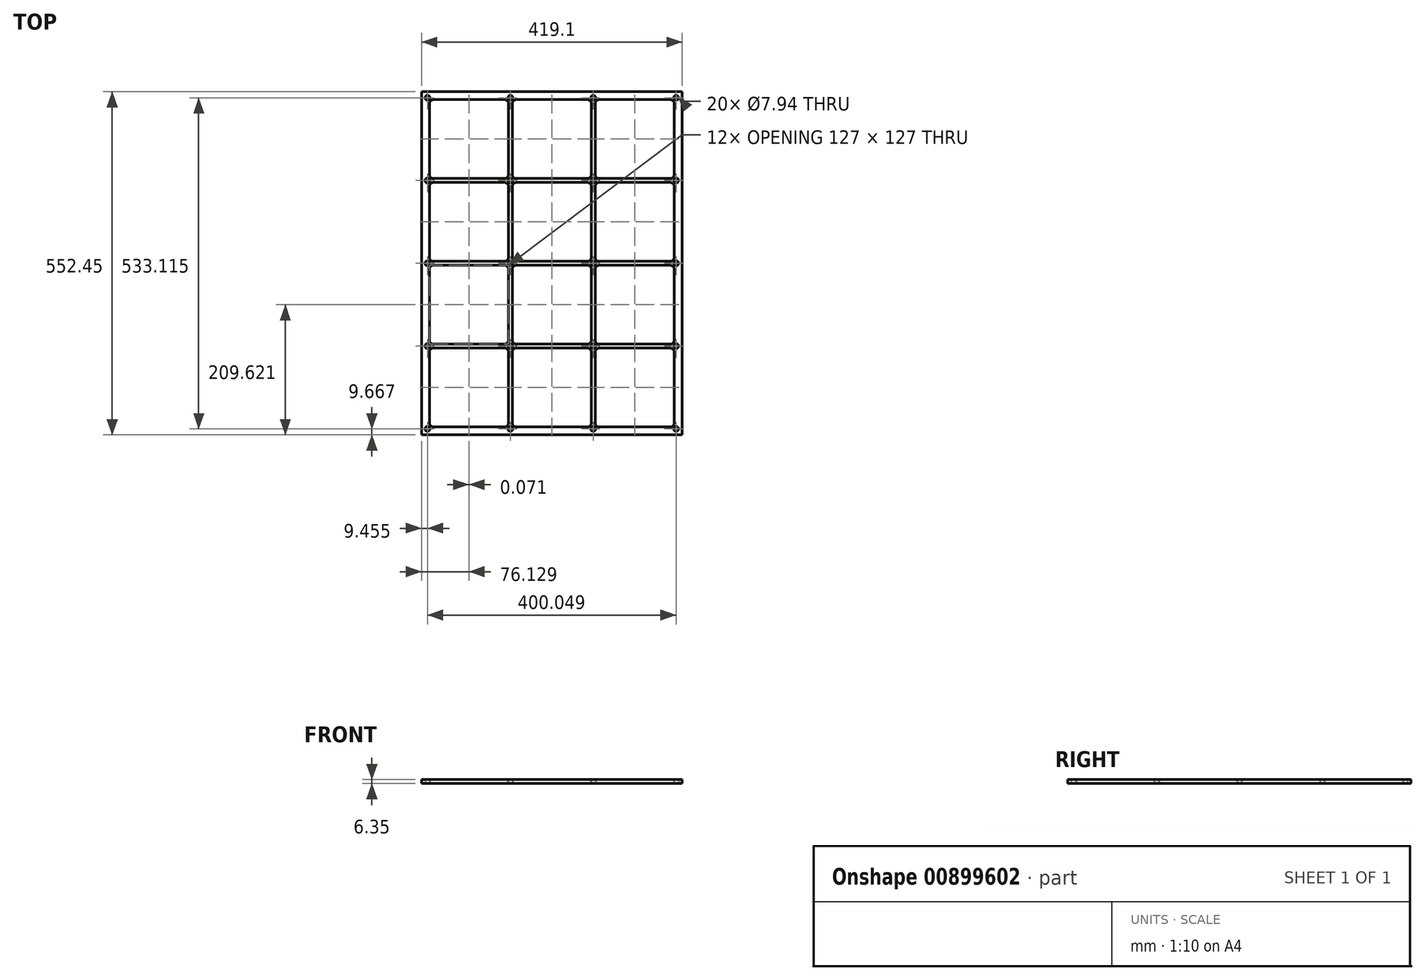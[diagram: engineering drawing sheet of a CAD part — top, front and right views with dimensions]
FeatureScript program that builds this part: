
annotation { "Feature Type Name" : "Feature", "Feature Type Description" : "" }
export const myFeature = defineFeature(function(context is Context, id is Id, definition is map)
    precondition{}
    {
        {
            var Q0;
            Q0=qCreatedBy(makeId("Top.planeOp"),FACE);
            var sketch = newSketch(context, id + "F0", { "sketchPlane" : qUnion([Q0])});
            skLineSegment(sketch, "E0.bottom", {"start": v(19.05, 12.84) * mm, "end": v(133.35, 12.84) * mm});
            skLineSegment(sketch, "E0.top", {"start": v(19.05, 139.84) * mm, "end": v(133.35, 139.84) * mm});
            skLineSegment(sketch, "E0.left", {"start": v(12.7, 19.2) * mm, "end": v(12.7, 133.5) * mm});
            skLineSegment(sketch, "E0.right", {"start": v(139.7, 19.2) * mm, "end": v(139.7, 133.5) * mm});
            skArc(sketch, "E1.filletArc", {"start": v(19.05, 139.84) * mm, "mid": v(14.56, 137.98) * mm, "end": v(12.7, 133.5) * mm});
            skArc(sketch, "E2.filletArc", {"start": v(139.7, 133.5) * mm, "mid": v(137.84, 137.98) * mm, "end": v(133.35, 139.84) * mm});
            skArc(sketch, "E3.filletArc", {"start": v(133.35, 12.84) * mm, "mid": v(137.84, 14.7) * mm, "end": v(139.7, 19.2) * mm});
            skArc(sketch, "E4.filletArc", {"start": v(12.7, 19.2) * mm, "mid": v(14.56, 14.7) * mm, "end": v(19.05, 12.84) * mm});
            skLineSegment(sketch, "E5.0.1.1", {"start": v(139.63, 152.47) * mm, "end": v(139.63, 266.77) * mm});
            skLineSegment(sketch, "E5.0.1.2", {"start": v(18.98, 146.12) * mm, "end": v(133.28, 146.12) * mm});
            skLineSegment(sketch, "E5.0.1.4", {"start": v(18.98, 273.12) * mm, "end": v(133.28, 273.12) * mm});
            skLineSegment(sketch, "E5.0.1.5", {"start": v(12.63, 152.47) * mm, "end": v(12.63, 266.77) * mm});
            skArc(sketch, "E5.0.1.8", {"start": v(139.63, 266.77) * mm, "mid": v(137.77, 271.26) * mm, "end": v(133.28, 273.12) * mm});
            skArc(sketch, "E5.0.1.9", {"start": v(18.98, 273.12) * mm, "mid": v(14.49, 271.26) * mm, "end": v(12.63, 266.77) * mm});
            skArc(sketch, "E5.0.1.10", {"start": v(12.63, 152.47) * mm, "mid": v(14.49, 147.98) * mm, "end": v(18.98, 146.12) * mm});
            skArc(sketch, "E5.0.1.11", {"start": v(133.28, 146.12) * mm, "mid": v(137.77, 147.98) * mm, "end": v(139.63, 152.47) * mm});
            skLineSegment(sketch, "E5.0.2.1", {"start": v(139.7, 285.75) * mm, "end": v(139.7, 400.05) * mm});
            skLineSegment(sketch, "E5.0.2.2", {"start": v(19.05, 279.4) * mm, "end": v(133.35, 279.4) * mm});
            skLineSegment(sketch, "E5.0.2.4", {"start": v(19.05, 406.4) * mm, "end": v(133.35, 406.4) * mm});
            skLineSegment(sketch, "E5.0.2.5", {"start": v(12.7, 285.75) * mm, "end": v(12.7, 400.05) * mm});
            skArc(sketch, "E5.0.2.8", {"start": v(139.7, 400.05) * mm, "mid": v(137.84, 404.54) * mm, "end": v(133.35, 406.4) * mm});
            skArc(sketch, "E5.0.2.9", {"start": v(19.05, 406.4) * mm, "mid": v(14.56, 404.54) * mm, "end": v(12.7, 400.05) * mm});
            skArc(sketch, "E5.0.2.10", {"start": v(12.7, 285.75) * mm, "mid": v(14.56, 281.26) * mm, "end": v(19.05, 279.4) * mm});
            skArc(sketch, "E5.0.2.11", {"start": v(133.35, 279.4) * mm, "mid": v(137.84, 281.26) * mm, "end": v(139.7, 285.75) * mm});
            skLineSegment(sketch, "E5.0.3.1", {"start": v(139.7, 419.1) * mm, "end": v(139.7, 533.4) * mm});
            skLineSegment(sketch, "E5.0.3.2", {"start": v(19.05, 412.75) * mm, "end": v(133.35, 412.75) * mm});
            skLineSegment(sketch, "E5.0.3.4", {"start": v(19.05, 539.75) * mm, "end": v(133.35, 539.75) * mm});
            skLineSegment(sketch, "E5.0.3.5", {"start": v(12.7, 419.1) * mm, "end": v(12.7, 533.4) * mm});
            skArc(sketch, "E5.0.3.8", {"start": v(139.7, 533.4) * mm, "mid": v(137.84, 537.9) * mm, "end": v(133.35, 539.75) * mm});
            skArc(sketch, "E5.0.3.9", {"start": v(19.05, 539.75) * mm, "mid": v(14.56, 537.9) * mm, "end": v(12.7, 533.4) * mm});
            skArc(sketch, "E5.0.3.10", {"start": v(12.7, 419.1) * mm, "mid": v(14.56, 414.6) * mm, "end": v(19.05, 412.75) * mm});
            skArc(sketch, "E5.0.3.11", {"start": v(133.35, 412.75) * mm, "mid": v(137.84, 414.6) * mm, "end": v(139.7, 419.1) * mm});
            skLineSegment(sketch, "E5.1.0.1", {"start": v(272.98, 19.12) * mm, "end": v(272.98, 133.42) * mm});
            skLineSegment(sketch, "E5.1.0.2", {"start": v(152.33, 12.77) * mm, "end": v(266.63, 12.77) * mm});
            skLineSegment(sketch, "E5.1.0.4", {"start": v(152.33, 139.77) * mm, "end": v(266.63, 139.77) * mm});
            skLineSegment(sketch, "E5.1.0.5", {"start": v(145.98, 19.12) * mm, "end": v(145.98, 133.42) * mm});
            skArc(sketch, "E5.1.0.8", {"start": v(272.98, 133.42) * mm, "mid": v(271.12, 137.91) * mm, "end": v(266.63, 139.77) * mm});
            skArc(sketch, "E5.1.0.9", {"start": v(152.33, 139.77) * mm, "mid": v(147.84, 137.91) * mm, "end": v(145.98, 133.42) * mm});
            skArc(sketch, "E5.1.0.10", {"start": v(145.98, 19.12) * mm, "mid": v(147.84, 14.63) * mm, "end": v(152.33, 12.77) * mm});
            skArc(sketch, "E5.1.0.11", {"start": v(266.63, 12.77) * mm, "mid": v(271.12, 14.63) * mm, "end": v(272.98, 19.12) * mm});
            skLineSegment(sketch, "E5.1.1.1", {"start": v(273.05, 152.54) * mm, "end": v(273.05, 266.84) * mm});
            skLineSegment(sketch, "E5.1.1.2", {"start": v(152.4, 146.2) * mm, "end": v(266.7, 146.2) * mm});
            skLineSegment(sketch, "E5.1.1.4", {"start": v(152.4, 273.2) * mm, "end": v(266.7, 273.2) * mm});
            skLineSegment(sketch, "E5.1.1.5", {"start": v(146.05, 152.54) * mm, "end": v(146.05, 266.84) * mm});
            skArc(sketch, "E5.1.1.8", {"start": v(273.05, 266.84) * mm, "mid": v(271.2, 271.33) * mm, "end": v(266.7, 273.2) * mm});
            skArc(sketch, "E5.1.1.9", {"start": v(152.4, 273.2) * mm, "mid": v(147.9, 271.33) * mm, "end": v(146.05, 266.84) * mm});
            skArc(sketch, "E5.1.1.10", {"start": v(146.05, 152.54) * mm, "mid": v(147.9, 148.05) * mm, "end": v(152.4, 146.2) * mm});
            skArc(sketch, "E5.1.1.11", {"start": v(266.7, 146.2) * mm, "mid": v(271.2, 148.05) * mm, "end": v(273.05, 152.54) * mm});
            skLineSegment(sketch, "E5.1.2.1", {"start": v(273.05, 285.75) * mm, "end": v(273.05, 400.05) * mm});
            skLineSegment(sketch, "E5.1.2.2", {"start": v(152.4, 279.4) * mm, "end": v(266.7, 279.4) * mm});
            skLineSegment(sketch, "E5.1.2.4", {"start": v(152.4, 406.4) * mm, "end": v(266.7, 406.4) * mm});
            skLineSegment(sketch, "E5.1.2.5", {"start": v(146.05, 285.75) * mm, "end": v(146.05, 400.05) * mm});
            skArc(sketch, "E5.1.2.8", {"start": v(273.05, 400.05) * mm, "mid": v(271.2, 404.54) * mm, "end": v(266.7, 406.4) * mm});
            skArc(sketch, "E5.1.2.9", {"start": v(152.4, 406.4) * mm, "mid": v(147.9, 404.54) * mm, "end": v(146.05, 400.05) * mm});
            skArc(sketch, "E5.1.2.10", {"start": v(146.05, 285.75) * mm, "mid": v(147.9, 281.26) * mm, "end": v(152.4, 279.4) * mm});
            skArc(sketch, "E5.1.2.11", {"start": v(266.7, 279.4) * mm, "mid": v(271.2, 281.26) * mm, "end": v(273.05, 285.75) * mm});
            skLineSegment(sketch, "E5.1.3.1", {"start": v(273.05, 419.1) * mm, "end": v(273.05, 533.4) * mm});
            skLineSegment(sketch, "E5.1.3.2", {"start": v(152.4, 412.75) * mm, "end": v(266.7, 412.75) * mm});
            skLineSegment(sketch, "E5.1.3.4", {"start": v(152.4, 539.75) * mm, "end": v(266.7, 539.75) * mm});
            skLineSegment(sketch, "E5.1.3.5", {"start": v(146.05, 419.1) * mm, "end": v(146.05, 533.4) * mm});
            skArc(sketch, "E5.1.3.8", {"start": v(273.05, 533.4) * mm, "mid": v(271.2, 537.9) * mm, "end": v(266.7, 539.75) * mm});
            skArc(sketch, "E5.1.3.9", {"start": v(152.4, 539.75) * mm, "mid": v(147.9, 537.9) * mm, "end": v(146.05, 533.4) * mm});
            skArc(sketch, "E5.1.3.10", {"start": v(146.05, 419.1) * mm, "mid": v(147.9, 414.6) * mm, "end": v(152.4, 412.75) * mm});
            skArc(sketch, "E5.1.3.11", {"start": v(266.7, 412.75) * mm, "mid": v(271.2, 414.6) * mm, "end": v(273.05, 419.1) * mm});
            skLineSegment(sketch, "E5.2.0.1", {"start": v(406.4, 19.05) * mm, "end": v(406.4, 133.35) * mm});
            skLineSegment(sketch, "E5.2.0.2", {"start": v(285.75, 12.7) * mm, "end": v(400.05, 12.7) * mm});
            skLineSegment(sketch, "E5.2.0.4", {"start": v(285.75, 139.7) * mm, "end": v(400.05, 139.7) * mm});
            skLineSegment(sketch, "E5.2.0.5", {"start": v(279.4, 19.05) * mm, "end": v(279.4, 133.35) * mm});
            skArc(sketch, "E5.2.0.8", {"start": v(406.4, 133.35) * mm, "mid": v(404.54, 137.84) * mm, "end": v(400.05, 139.7) * mm});
            skArc(sketch, "E5.2.0.9", {"start": v(285.75, 139.7) * mm, "mid": v(281.26, 137.84) * mm, "end": v(279.4, 133.35) * mm});
            skArc(sketch, "E5.2.0.10", {"start": v(279.4, 19.05) * mm, "mid": v(281.26, 14.56) * mm, "end": v(285.75, 12.7) * mm});
            skArc(sketch, "E5.2.0.11", {"start": v(400.05, 12.7) * mm, "mid": v(404.54, 14.56) * mm, "end": v(406.4, 19.05) * mm});
            skLineSegment(sketch, "E5.2.1.1", {"start": v(406.4, 152.4) * mm, "end": v(406.4, 266.7) * mm});
            skLineSegment(sketch, "E5.2.1.2", {"start": v(285.75, 146.05) * mm, "end": v(400.05, 146.05) * mm});
            skLineSegment(sketch, "E5.2.1.4", {"start": v(285.75, 273.05) * mm, "end": v(400.05, 273.05) * mm});
            skLineSegment(sketch, "E5.2.1.5", {"start": v(279.4, 152.4) * mm, "end": v(279.4, 266.7) * mm});
            skArc(sketch, "E5.2.1.8", {"start": v(406.4, 266.7) * mm, "mid": v(404.54, 271.2) * mm, "end": v(400.05, 273.05) * mm});
            skArc(sketch, "E5.2.1.9", {"start": v(285.75, 273.05) * mm, "mid": v(281.26, 271.2) * mm, "end": v(279.4, 266.7) * mm});
            skArc(sketch, "E5.2.1.10", {"start": v(279.4, 152.4) * mm, "mid": v(281.26, 147.9) * mm, "end": v(285.75, 146.05) * mm});
            skArc(sketch, "E5.2.1.11", {"start": v(400.05, 146.05) * mm, "mid": v(404.54, 147.9) * mm, "end": v(406.4, 152.4) * mm});
            skLineSegment(sketch, "E5.2.2.1", {"start": v(406.4, 285.75) * mm, "end": v(406.4, 400.05) * mm});
            skLineSegment(sketch, "E5.2.2.2", {"start": v(285.75, 279.4) * mm, "end": v(400.05, 279.4) * mm});
            skLineSegment(sketch, "E5.2.2.4", {"start": v(285.75, 406.4) * mm, "end": v(400.05, 406.4) * mm});
            skLineSegment(sketch, "E5.2.2.5", {"start": v(279.4, 285.75) * mm, "end": v(279.4, 400.05) * mm});
            skArc(sketch, "E5.2.2.8", {"start": v(406.4, 400.05) * mm, "mid": v(404.54, 404.54) * mm, "end": v(400.05, 406.4) * mm});
            skArc(sketch, "E5.2.2.9", {"start": v(285.75, 406.4) * mm, "mid": v(281.26, 404.54) * mm, "end": v(279.4, 400.05) * mm});
            skArc(sketch, "E5.2.2.10", {"start": v(279.4, 285.75) * mm, "mid": v(281.26, 281.26) * mm, "end": v(285.75, 279.4) * mm});
            skArc(sketch, "E5.2.2.11", {"start": v(400.05, 279.4) * mm, "mid": v(404.54, 281.26) * mm, "end": v(406.4, 285.75) * mm});
            skLineSegment(sketch, "E5.2.3.1", {"start": v(406.4, 419.1) * mm, "end": v(406.4, 533.4) * mm});
            skLineSegment(sketch, "E5.2.3.2", {"start": v(285.75, 412.75) * mm, "end": v(400.05, 412.75) * mm});
            skLineSegment(sketch, "E5.2.3.4", {"start": v(285.75, 539.75) * mm, "end": v(400.05, 539.75) * mm});
            skLineSegment(sketch, "E5.2.3.5", {"start": v(279.4, 419.1) * mm, "end": v(279.4, 533.4) * mm});
            skArc(sketch, "E5.2.3.8", {"start": v(406.4, 533.4) * mm, "mid": v(404.54, 537.9) * mm, "end": v(400.05, 539.75) * mm});
            skArc(sketch, "E5.2.3.9", {"start": v(285.75, 539.75) * mm, "mid": v(281.26, 537.9) * mm, "end": v(279.4, 533.4) * mm});
            skArc(sketch, "E5.2.3.10", {"start": v(279.4, 419.1) * mm, "mid": v(281.26, 414.6) * mm, "end": v(285.75, 412.75) * mm});
            skArc(sketch, "E5.2.3.11", {"start": v(400.05, 412.75) * mm, "mid": v(404.54, 414.6) * mm, "end": v(406.4, 419.1) * mm});
            skLineSegment(sketch, "E6.bottom", {"start": v(0, 0) * mm, "end": v(419.1, 0) * mm});
            skLineSegment(sketch, "E6.top", {"start": v(0, 552.45) * mm, "end": v(419.1, 552.45) * mm});
            skLineSegment(sketch, "E6.left", {"start": v(0, 0) * mm, "end": v(0, 552.45) * mm});
            skLineSegment(sketch, "E6.right", {"start": v(419.1, 0) * mm, "end": v(419.1, 552.45) * mm});
            skLineSegment(sketch, "E7", {"start": v(133.28, 152.47) * mm, "end": v(152.33, 133.42) * mm, "construction": true});
            skLineSegment(sketch, "E8", {"start": v(152.4, 152.54) * mm, "end": v(133.35, 133.5) * mm, "construction": true});
            skLineSegment(sketch, "E9.bottom", {"start": v(13.42, 13.64) * mm, "end": v(5.49, 13.64) * mm, "construction": true});
            skLineSegment(sketch, "E9.top", {"start": v(13.42, 5.7) * mm, "end": v(5.49, 5.7) * mm, "construction": true});
            skLineSegment(sketch, "E9.left", {"start": v(13.42, 13.64) * mm, "end": v(13.42, 5.7) * mm, "construction": true});
            skLineSegment(sketch, "E9.right", {"start": v(5.49, 13.64) * mm, "end": v(5.49, 5.7) * mm, "construction": true});
            skPoint(sketch, "E9.middle", {"position": v(142.8, 142.95) * mm});
            skCircle(sketch, "E10", {"center": v(9.45, 9.67) * mm, "radius": 3.97 * mm});
            skLineSegment(sketch, "E11", {"start": v(266.63, 133.42) * mm, "end": v(285.75, 152.4) * mm, "construction": true});
            skLineSegment(sketch, "E12", {"start": v(285.75, 133.35) * mm, "end": v(266.7, 152.54) * mm, "construction": true});
            skLineSegment(sketch, "E13", {"start": v(133.35, 285.75) * mm, "end": v(152.4, 266.84) * mm, "construction": true});
            skLineSegment(sketch, "E14", {"start": v(133.28, 266.77) * mm, "end": v(152.4, 285.75) * mm, "construction": true});
            skLineSegment(sketch, "E15", {"start": v(266.7, 285.75) * mm, "end": v(285.75, 266.7) * mm, "construction": true});
            skLineSegment(sketch, "E16", {"start": v(285.75, 285.75) * mm, "end": v(266.7, 266.84) * mm, "construction": true});
            skLineSegment(sketch, "E17", {"start": v(142.84, 276.26) * mm, "end": v(276.19, 276.26) * mm, "construction": true});
            skLineSegment(sketch, "E18", {"start": v(276.19, 276.26) * mm, "end": v(276.19, 142.98) * mm, "construction": true});
            skLineSegment(sketch, "E19.0.1.0", {"start": v(13.42, 138.98) * mm, "end": v(5.49, 138.98) * mm, "construction": true});
            skLineSegment(sketch, "E19.0.1.1", {"start": v(13.42, 146.91) * mm, "end": v(5.49, 146.91) * mm, "construction": true});
            skLineSegment(sketch, "E19.0.1.2", {"start": v(5.49, 146.91) * mm, "end": v(5.49, 138.98) * mm, "construction": true});
            skLineSegment(sketch, "E19.0.1.3", {"start": v(13.42, 146.91) * mm, "end": v(13.42, 138.98) * mm, "construction": true});
            skCircle(sketch, "E19.0.1.4", {"center": v(9.45, 142.95) * mm, "radius": 3.97 * mm});
            skLineSegment(sketch, "E19.1.0.0", {"start": v(146.77, 5.7) * mm, "end": v(138.84, 5.7) * mm, "construction": true});
            skLineSegment(sketch, "E19.1.0.1", {"start": v(146.77, 13.64) * mm, "end": v(138.84, 13.64) * mm, "construction": true});
            skLineSegment(sketch, "E19.1.0.2", {"start": v(138.84, 13.64) * mm, "end": v(138.84, 5.7) * mm, "construction": true});
            skLineSegment(sketch, "E19.1.0.3", {"start": v(146.77, 13.64) * mm, "end": v(146.77, 5.7) * mm, "construction": true});
            skCircle(sketch, "E19.1.0.4", {"center": v(142.8, 9.67) * mm, "radius": 3.97 * mm});
            skLineSegment(sketch, "E19.1.1.0", {"start": v(146.77, 138.98) * mm, "end": v(138.84, 138.98) * mm, "construction": true});
            skLineSegment(sketch, "E19.1.1.1", {"start": v(146.77, 146.91) * mm, "end": v(138.84, 146.91) * mm, "construction": true});
            skLineSegment(sketch, "E19.1.1.2", {"start": v(138.84, 146.91) * mm, "end": v(138.84, 138.98) * mm, "construction": true});
            skLineSegment(sketch, "E19.1.1.3", {"start": v(146.77, 146.91) * mm, "end": v(146.77, 138.98) * mm, "construction": true});
            skCircle(sketch, "E19.1.1.4", {"center": v(142.8, 142.95) * mm, "radius": 3.97 * mm});
            skLineSegment(sketch, "E19.2.0.0", {"start": v(280.12, 5.7) * mm, "end": v(272.19, 5.7) * mm, "construction": true});
            skLineSegment(sketch, "E19.2.0.1", {"start": v(280.12, 13.64) * mm, "end": v(272.19, 13.64) * mm, "construction": true});
            skLineSegment(sketch, "E19.2.0.2", {"start": v(272.19, 13.64) * mm, "end": v(272.19, 5.7) * mm, "construction": true});
            skLineSegment(sketch, "E19.2.0.3", {"start": v(280.12, 13.64) * mm, "end": v(280.12, 5.7) * mm, "construction": true});
            skCircle(sketch, "E19.2.0.4", {"center": v(276.15, 9.67) * mm, "radius": 3.97 * mm});
            skLineSegment(sketch, "E19.2.1.0", {"start": v(280.12, 138.98) * mm, "end": v(272.19, 138.98) * mm, "construction": true});
            skLineSegment(sketch, "E19.2.1.1", {"start": v(280.12, 146.91) * mm, "end": v(272.19, 146.91) * mm, "construction": true});
            skLineSegment(sketch, "E19.2.1.2", {"start": v(272.19, 146.91) * mm, "end": v(272.19, 138.98) * mm, "construction": true});
            skLineSegment(sketch, "E19.2.1.3", {"start": v(280.12, 146.91) * mm, "end": v(280.12, 138.98) * mm, "construction": true});
            skCircle(sketch, "E19.2.1.4", {"center": v(276.15, 142.95) * mm, "radius": 3.97 * mm});
            skLineSegment(sketch, "E19.3.0.0", {"start": v(413.47, 5.7) * mm, "end": v(405.54, 5.7) * mm, "construction": true});
            skLineSegment(sketch, "E19.3.0.1", {"start": v(413.47, 13.64) * mm, "end": v(405.54, 13.64) * mm, "construction": true});
            skLineSegment(sketch, "E19.3.0.2", {"start": v(405.54, 13.64) * mm, "end": v(405.54, 5.7) * mm, "construction": true});
            skLineSegment(sketch, "E19.3.0.3", {"start": v(413.47, 13.64) * mm, "end": v(413.47, 5.7) * mm, "construction": true});
            skCircle(sketch, "E19.3.0.4", {"center": v(409.5, 9.67) * mm, "radius": 3.97 * mm});
            skLineSegment(sketch, "E19.3.1.0", {"start": v(413.47, 138.98) * mm, "end": v(405.54, 138.98) * mm, "construction": true});
            skLineSegment(sketch, "E19.3.1.1", {"start": v(413.47, 146.91) * mm, "end": v(405.54, 146.91) * mm, "construction": true});
            skLineSegment(sketch, "E19.3.1.2", {"start": v(405.54, 146.91) * mm, "end": v(405.54, 138.98) * mm, "construction": true});
            skLineSegment(sketch, "E19.3.1.3", {"start": v(413.47, 146.91) * mm, "end": v(413.47, 138.98) * mm, "construction": true});
            skCircle(sketch, "E19.3.1.4", {"center": v(409.5, 142.95) * mm, "radius": 3.97 * mm});
            skLineSegment(sketch, "E20.0.0.2", {"start": v(13.42, 272.26) * mm, "end": v(5.49, 272.26) * mm, "construction": true});
            skLineSegment(sketch, "E20.3.0.2", {"start": v(13.42, 280.2) * mm, "end": v(5.49, 280.2) * mm, "construction": true});
            skLineSegment(sketch, "E20.6.0.2", {"start": v(5.49, 280.2) * mm, "end": v(5.49, 272.26) * mm, "construction": true});
            skLineSegment(sketch, "E20.9.0.2", {"start": v(13.42, 280.2) * mm, "end": v(13.42, 272.26) * mm, "construction": true});
            skCircle(sketch, "E20.12.0.2", {"center": v(9.45, 276.22) * mm, "radius": 3.97 * mm});
            skLineSegment(sketch, "E20.0.0.3", {"start": v(13.42, 405.53) * mm, "end": v(5.49, 405.53) * mm, "construction": true});
            skLineSegment(sketch, "E20.3.0.3", {"start": v(13.42, 413.47) * mm, "end": v(5.49, 413.47) * mm, "construction": true});
            skLineSegment(sketch, "E20.6.0.3", {"start": v(5.49, 413.47) * mm, "end": v(5.49, 405.53) * mm, "construction": true});
            skLineSegment(sketch, "E20.9.0.3", {"start": v(13.42, 413.47) * mm, "end": v(13.42, 405.53) * mm, "construction": true});
            skCircle(sketch, "E20.12.0.3", {"center": v(9.45, 409.5) * mm, "radius": 3.97 * mm});
            skLineSegment(sketch, "E20.0.0.4", {"start": v(13.42, 538.81) * mm, "end": v(5.49, 538.81) * mm, "construction": true});
            skLineSegment(sketch, "E20.3.0.4", {"start": v(13.42, 546.75) * mm, "end": v(5.49, 546.75) * mm, "construction": true});
            skLineSegment(sketch, "E20.6.0.4", {"start": v(5.49, 546.75) * mm, "end": v(5.49, 538.81) * mm, "construction": true});
            skLineSegment(sketch, "E20.9.0.4", {"start": v(13.42, 546.75) * mm, "end": v(13.42, 538.81) * mm, "construction": true});
            skCircle(sketch, "E20.12.0.4", {"center": v(9.45, 542.78) * mm, "radius": 3.97 * mm});
            skLineSegment(sketch, "E20.0.1.2", {"start": v(146.77, 272.26) * mm, "end": v(138.84, 272.26) * mm, "construction": true});
            skLineSegment(sketch, "E20.3.1.2", {"start": v(146.77, 280.2) * mm, "end": v(138.84, 280.2) * mm, "construction": true});
            skLineSegment(sketch, "E20.6.1.2", {"start": v(138.84, 280.2) * mm, "end": v(138.84, 272.26) * mm, "construction": true});
            skLineSegment(sketch, "E20.9.1.2", {"start": v(146.77, 280.2) * mm, "end": v(146.77, 272.26) * mm, "construction": true});
            skCircle(sketch, "E20.12.1.2", {"center": v(142.8, 276.22) * mm, "radius": 3.97 * mm});
            skLineSegment(sketch, "E20.0.1.3", {"start": v(146.77, 405.53) * mm, "end": v(138.84, 405.53) * mm, "construction": true});
            skLineSegment(sketch, "E20.3.1.3", {"start": v(146.77, 413.47) * mm, "end": v(138.84, 413.47) * mm, "construction": true});
            skLineSegment(sketch, "E20.6.1.3", {"start": v(138.84, 413.47) * mm, "end": v(138.84, 405.53) * mm, "construction": true});
            skLineSegment(sketch, "E20.9.1.3", {"start": v(146.77, 413.47) * mm, "end": v(146.77, 405.53) * mm, "construction": true});
            skCircle(sketch, "E20.12.1.3", {"center": v(142.8, 409.5) * mm, "radius": 3.97 * mm});
            skLineSegment(sketch, "E20.0.1.4", {"start": v(146.77, 538.81) * mm, "end": v(138.84, 538.81) * mm, "construction": true});
            skLineSegment(sketch, "E20.3.1.4", {"start": v(146.77, 546.75) * mm, "end": v(138.84, 546.75) * mm, "construction": true});
            skLineSegment(sketch, "E20.6.1.4", {"start": v(138.84, 546.75) * mm, "end": v(138.84, 538.81) * mm, "construction": true});
            skLineSegment(sketch, "E20.9.1.4", {"start": v(146.77, 546.75) * mm, "end": v(146.77, 538.81) * mm, "construction": true});
            skCircle(sketch, "E20.12.1.4", {"center": v(142.8, 542.78) * mm, "radius": 3.97 * mm});
            skLineSegment(sketch, "E20.0.2.2", {"start": v(280.12, 272.26) * mm, "end": v(272.19, 272.26) * mm, "construction": true});
            skLineSegment(sketch, "E20.3.2.2", {"start": v(280.12, 280.2) * mm, "end": v(272.19, 280.2) * mm, "construction": true});
            skLineSegment(sketch, "E20.6.2.2", {"start": v(272.19, 280.2) * mm, "end": v(272.19, 272.26) * mm, "construction": true});
            skLineSegment(sketch, "E20.9.2.2", {"start": v(280.12, 280.2) * mm, "end": v(280.12, 272.26) * mm, "construction": true});
            skCircle(sketch, "E20.12.2.2", {"center": v(276.15, 276.22) * mm, "radius": 3.97 * mm});
            skLineSegment(sketch, "E20.0.2.3", {"start": v(280.12, 405.53) * mm, "end": v(272.19, 405.53) * mm, "construction": true});
            skLineSegment(sketch, "E20.3.2.3", {"start": v(280.12, 413.47) * mm, "end": v(272.19, 413.47) * mm, "construction": true});
            skLineSegment(sketch, "E20.6.2.3", {"start": v(272.19, 413.47) * mm, "end": v(272.19, 405.53) * mm, "construction": true});
            skLineSegment(sketch, "E20.9.2.3", {"start": v(280.12, 413.47) * mm, "end": v(280.12, 405.53) * mm, "construction": true});
            skCircle(sketch, "E20.12.2.3", {"center": v(276.15, 409.5) * mm, "radius": 3.97 * mm});
            skLineSegment(sketch, "E20.0.2.4", {"start": v(280.12, 538.81) * mm, "end": v(272.19, 538.81) * mm, "construction": true});
            skLineSegment(sketch, "E20.3.2.4", {"start": v(280.12, 546.75) * mm, "end": v(272.19, 546.75) * mm, "construction": true});
            skLineSegment(sketch, "E20.6.2.4", {"start": v(272.19, 546.75) * mm, "end": v(272.19, 538.81) * mm, "construction": true});
            skLineSegment(sketch, "E20.9.2.4", {"start": v(280.12, 546.75) * mm, "end": v(280.12, 538.81) * mm, "construction": true});
            skCircle(sketch, "E20.12.2.4", {"center": v(276.15, 542.78) * mm, "radius": 3.97 * mm});
            skLineSegment(sketch, "E20.0.3.2", {"start": v(413.47, 272.26) * mm, "end": v(405.54, 272.26) * mm, "construction": true});
            skLineSegment(sketch, "E20.3.3.2", {"start": v(413.47, 280.2) * mm, "end": v(405.54, 280.2) * mm, "construction": true});
            skLineSegment(sketch, "E20.6.3.2", {"start": v(405.54, 280.2) * mm, "end": v(405.54, 272.26) * mm, "construction": true});
            skLineSegment(sketch, "E20.9.3.2", {"start": v(413.47, 280.2) * mm, "end": v(413.47, 272.26) * mm, "construction": true});
            skCircle(sketch, "E20.12.3.2", {"center": v(409.5, 276.22) * mm, "radius": 3.97 * mm});
            skLineSegment(sketch, "E20.0.3.3", {"start": v(413.47, 405.53) * mm, "end": v(405.54, 405.53) * mm, "construction": true});
            skLineSegment(sketch, "E20.3.3.3", {"start": v(413.47, 413.47) * mm, "end": v(405.54, 413.47) * mm, "construction": true});
            skLineSegment(sketch, "E20.6.3.3", {"start": v(405.54, 413.47) * mm, "end": v(405.54, 405.53) * mm, "construction": true});
            skLineSegment(sketch, "E20.9.3.3", {"start": v(413.47, 413.47) * mm, "end": v(413.47, 405.53) * mm, "construction": true});
            skCircle(sketch, "E20.12.3.3", {"center": v(409.5, 409.5) * mm, "radius": 3.97 * mm});
            skLineSegment(sketch, "E20.0.3.4", {"start": v(413.47, 538.81) * mm, "end": v(405.54, 538.81) * mm, "construction": true});
            skLineSegment(sketch, "E20.3.3.4", {"start": v(413.47, 546.75) * mm, "end": v(405.54, 546.75) * mm, "construction": true});
            skLineSegment(sketch, "E20.6.3.4", {"start": v(405.54, 546.75) * mm, "end": v(405.54, 538.81) * mm, "construction": true});
            skLineSegment(sketch, "E20.9.3.4", {"start": v(413.47, 546.75) * mm, "end": v(413.47, 538.81) * mm, "construction": true});
            skCircle(sketch, "E20.12.3.4", {"center": v(409.5, 542.78) * mm, "radius": 3.97 * mm});
            skSolve(sketch);
        }
        {
            var Q0;
            Q0=makeQuery(id+"F0.imprint","IMPRINT",FACE,{"disambiguationData":[TD([[makeQuery(id+"F0.imprint","IMPRINT",EDGE,{"derivedFrom":sQuery(id+"F0.wireOp",EDGE,"E0.bottom")}),-1.0]])]});
            extrude(context, id + "F1", {"entities" : qUnion([Q0]), "depth" : 6.35 * mm, "offsetDistance" : 25.4 * mm});
        }
    });
